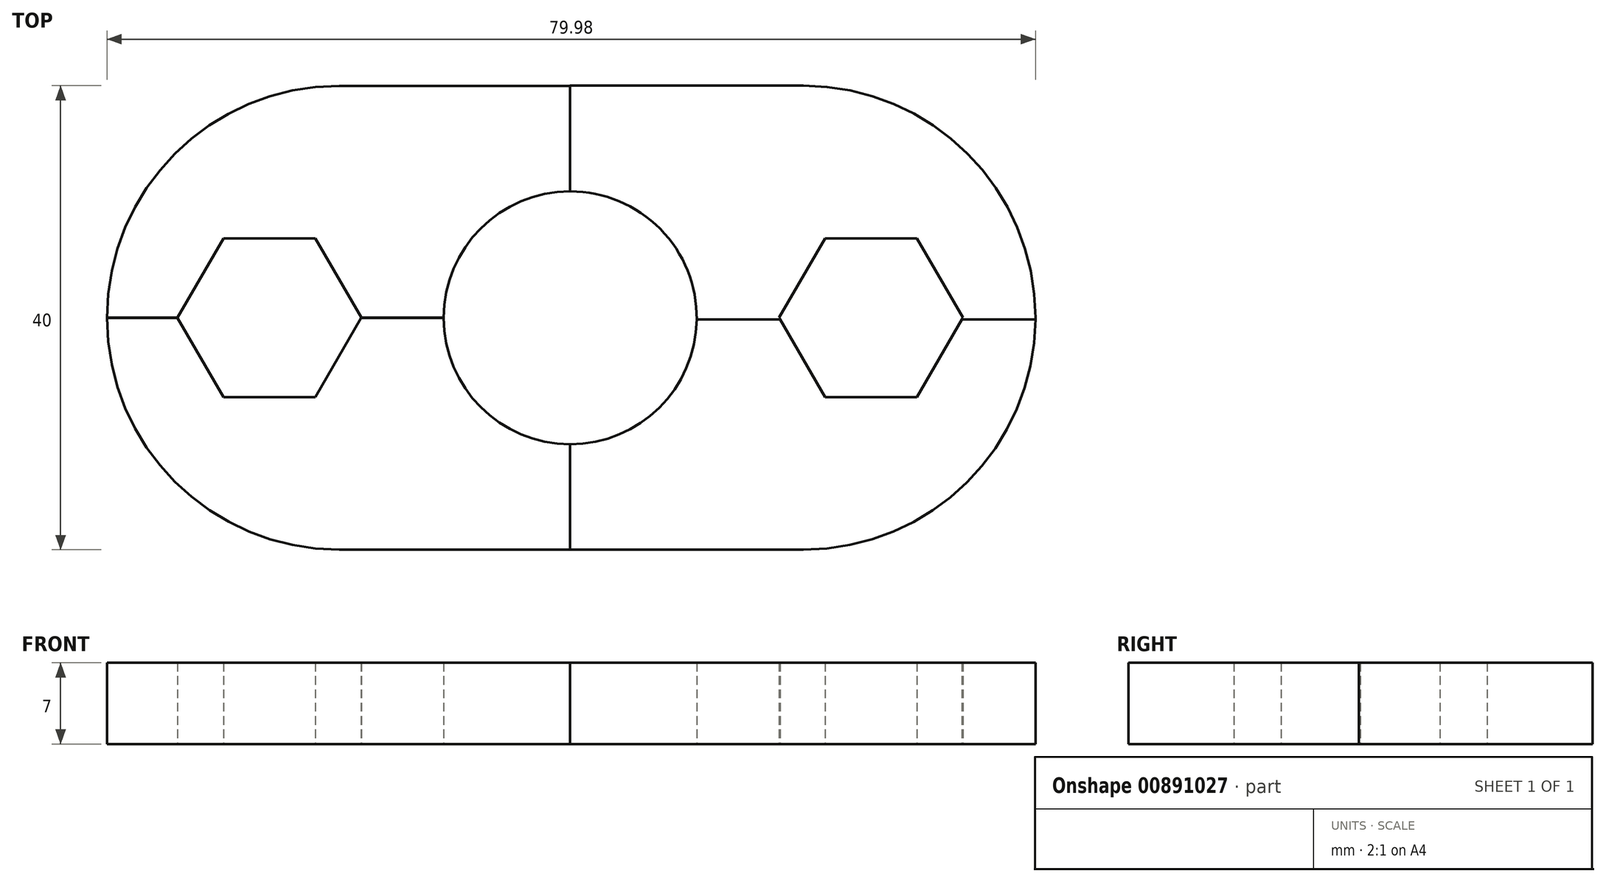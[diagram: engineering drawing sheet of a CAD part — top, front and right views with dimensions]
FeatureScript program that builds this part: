
annotation { "Feature Type Name" : "Feature", "Feature Type Description" : "" }
export const myFeature = defineFeature(function(context is Context, id is Id, definition is map)
    precondition{}
    {
        {
            var Q0;
            Q0=qCreatedBy(makeId("Top.planeOp"),FACE);
            var sketch = newSketch(context, id + "F0", { "sketchPlane" : qUnion([Q0])});
            skCircle(sketch, "E0.cCircle", {"center": v(-25.9, 0) * mm, "radius": 6.85 * mm, "construction": true});
            skLineSegment(sketch, "E0.0", {"start": v(-33.82, 0) * mm, "end": v(-29.86, 6.85) * mm});
            skLineSegment(sketch, "E0.1", {"start": v(-29.86, 6.85) * mm, "end": v(-21.95, 6.85) * mm});
            skLineSegment(sketch, "E0.2", {"start": v(-21.95, 6.85) * mm, "end": v(-18, 0) * mm});
            skLineSegment(sketch, "E0.3", {"start": v(-18, 0) * mm, "end": v(-21.95, -6.85) * mm});
            skLineSegment(sketch, "E0.4", {"start": v(-21.95, -6.85) * mm, "end": v(-29.86, -6.85) * mm});
            skLineSegment(sketch, "E0.5", {"start": v(-29.86, -6.85) * mm, "end": v(-33.82, 0) * mm});
            skPoint(sketch, "E0.0.midPoint", {"position": v(-31.84, 3.42) * mm});
            skCircle(sketch, "E1", {"center": v(0, 0) * mm, "radius": 10.9 * mm});
            skCircle(sketch, "E2.cCircle", {"center": v(25.9, 0) * mm, "radius": 6.85 * mm, "construction": true});
            skLineSegment(sketch, "E2.0", {"start": v(29.86, -6.85) * mm, "end": v(21.95, -6.85) * mm});
            skLineSegment(sketch, "E2.1", {"start": v(21.95, -6.85) * mm, "end": v(18, 0) * mm});
            skLineSegment(sketch, "E2.2", {"start": v(18, 0) * mm, "end": v(21.95, 6.85) * mm});
            skLineSegment(sketch, "E2.3", {"start": v(21.95, 6.85) * mm, "end": v(29.86, 6.85) * mm});
            skLineSegment(sketch, "E2.4", {"start": v(29.86, 6.85) * mm, "end": v(33.82, 0) * mm});
            skLineSegment(sketch, "E2.5", {"start": v(33.82, 0) * mm, "end": v(29.86, -6.85) * mm});
            skPoint(sketch, "E2.0.midPoint", {"position": v(25.9, -6.85) * mm});
            skLineSegment(sketch, "E3.bottom", {"start": v(-39.9, 0) * mm, "end": v(0, 0) * mm});
            skLineSegment(sketch, "E3.top", {"start": v(-39.9, 20) * mm, "end": v(0, 20) * mm});
            skLineSegment(sketch, "E3.left", {"start": v(-39.9, 0) * mm, "end": v(-39.9, 20) * mm});
            skLineSegment(sketch, "E3.right", {"start": v(0, 0) * mm, "end": v(0, 20) * mm});
            skLineSegment(sketch, "E4.bottom", {"start": v(-39.9, -20) * mm, "end": v(0, -20) * mm});
            skLineSegment(sketch, "E4.left", {"start": v(-39.9, -20) * mm, "end": v(-39.9, 0) * mm});
            skLineSegment(sketch, "E4.right", {"start": v(0, -20) * mm, "end": v(0, 0) * mm});
            skLineSegment(sketch, "E5.bottom", {"start": v(0, -0.14) * mm, "end": v(40.08, -0.14) * mm});
            skLineSegment(sketch, "E5.top", {"start": v(0, 20) * mm, "end": v(40.08, 20) * mm});
            skLineSegment(sketch, "E5.left", {"start": v(0, -0.14) * mm, "end": v(0, 20) * mm});
            skLineSegment(sketch, "E5.right", {"start": v(40.08, -0.14) * mm, "end": v(40.08, 20) * mm});
            skLineSegment(sketch, "E6.bottom", {"start": v(0, -20) * mm, "end": v(40.08, -20) * mm});
            skLineSegment(sketch, "E6.left", {"start": v(0, -20) * mm, "end": v(0, -0.14) * mm});
            skLineSegment(sketch, "E6.right", {"start": v(40.08, -20) * mm, "end": v(40.08, -0.14) * mm});
            skSolve(sketch);
        }
        {
            var Q0;
            {var subQ13=sQuery(id+"F0.wireOp",EDGE,"E2.2");Q0=makeQuery(id+"F0.imprint","IMPRINT",FACE,{"disambiguationData":[TD([[makeQuery(id+"F0.imprint","IMPRINT",EDGE,{"derivedFrom":subQ13}),1.0]])]});}
            var Q1;
            {var subQ9=sQuery(id+"F0.wireOp",EDGE,"E0.0");Q1=makeQuery(id+"F0.imprint","IMPRINT",FACE,{"disambiguationData":[TD([[makeQuery(id+"F0.imprint","IMPRINT",EDGE,{"derivedFrom":subQ9}),1.0]])]});}
            var Q2;
            {var subQ6=sQuery(id+"F0.wireOp",EDGE,"E0.4");Q2=makeQuery(id+"F0.imprint","IMPRINT",FACE,{"disambiguationData":[TD([[makeQuery(id+"F0.imprint","IMPRINT",EDGE,{"derivedFrom":subQ6}),1.0]])]});}
            var Q3;
            {var subQ15=sQuery(id+"F0.wireOp",EDGE,"E2.0");Q3=makeQuery(id+"F0.imprint","IMPRINT",FACE,{"disambiguationData":[TD([[makeQuery(id+"F0.imprint","IMPRINT",EDGE,{"derivedFrom":subQ15}),1.0]])]});}
            extrude(context, id + "F1", {"entities" : qUnion([Q0, Q1, Q2, Q3]), "depth" : 7 * mm, "offsetDistance" : 25 * mm});
        }
        {
            var Q0;
            Q0=makeQuery(id+"F1.opExtrude","SWEPT_EDGE",EDGE,{"disambiguationData":[OSD([sQuery(id+"F0.wireOp",EDGE,"E3.top"),sQuery(id+"F0.wireOp",EDGE,"E3.left")])]});
            var Q1;
            Q1=makeQuery(id+"F1.opExtrude","SWEPT_EDGE",EDGE,{"disambiguationData":[OSD([sQuery(id+"F0.wireOp",EDGE,"E4.bottom"),sQuery(id+"F0.wireOp",EDGE,"E4.left")])]});
            var Q2;
            Q2=makeQuery(id+"F1.opExtrude","SWEPT_EDGE",EDGE,{"disambiguationData":[OSD([sQuery(id+"F0.wireOp",EDGE,"E6.bottom"),sQuery(id+"F0.wireOp",EDGE,"E6.right")])]});
            var Q3;
            Q3=makeQuery(id+"F1.opExtrude","SWEPT_EDGE",EDGE,{"disambiguationData":[OSD([sQuery(id+"F0.wireOp",EDGE,"E5.top"),sQuery(id+"F0.wireOp",EDGE,"E5.right")])]});
            fillet(context, id + "F2", {"entities" : qUnion([Q0, Q1, Q2, Q3]), "radius" : 20 * mm, "tangentPropagation" : true, "allowEdgeOverflow" : false});
        }
    });
